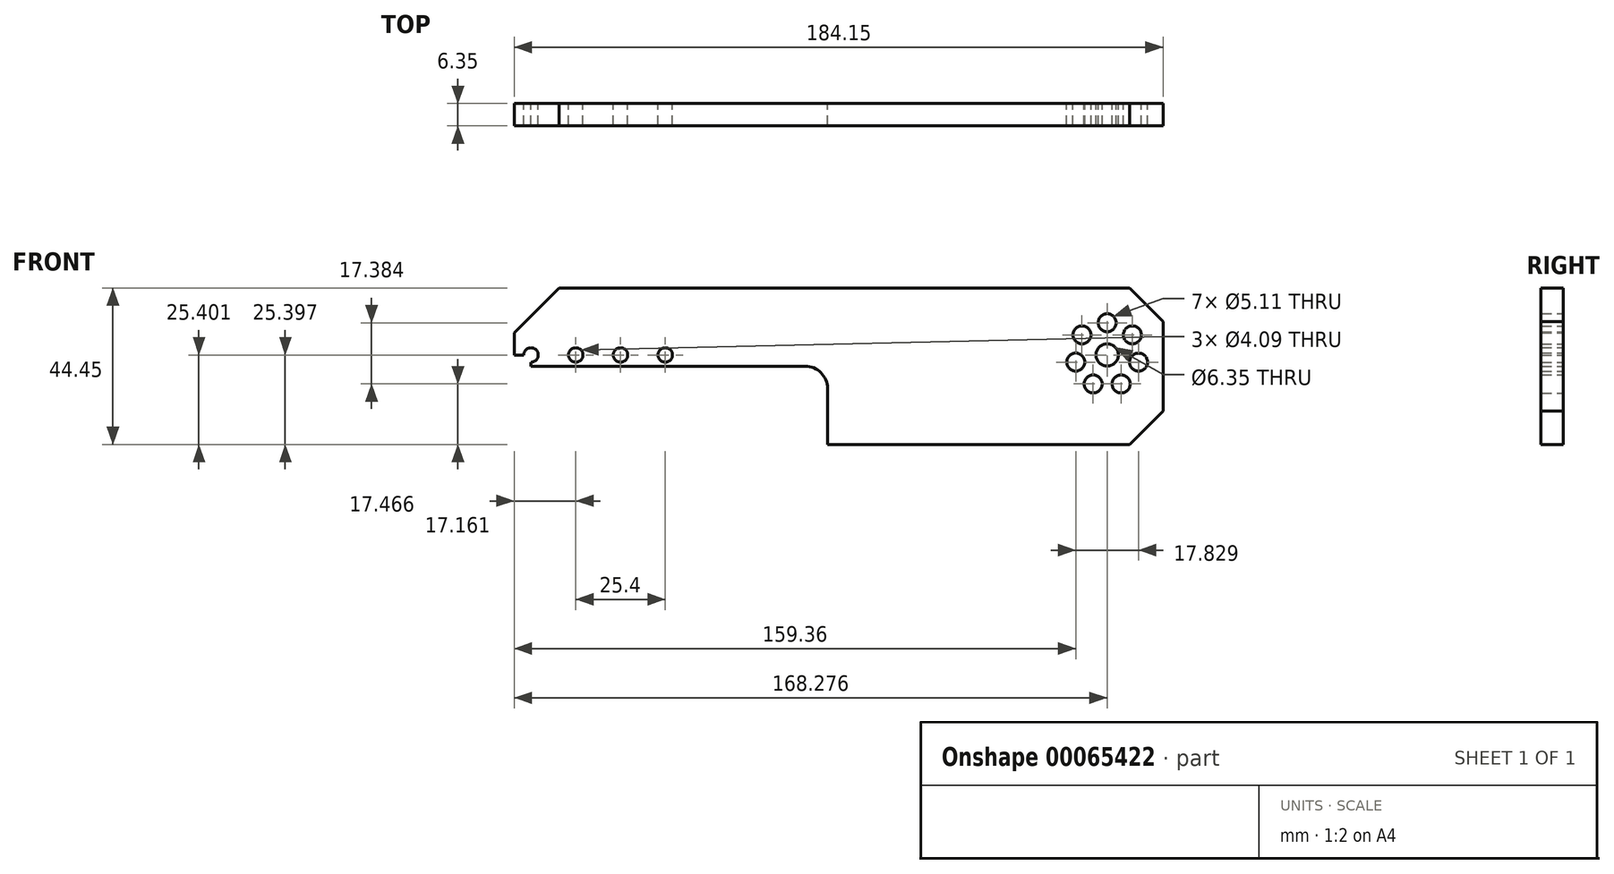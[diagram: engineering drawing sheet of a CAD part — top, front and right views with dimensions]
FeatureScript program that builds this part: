
annotation { "Feature Type Name" : "Feature", "Feature Type Description" : "" }
export const myFeature = defineFeature(function(context is Context, id is Id, definition is map)
    precondition{}
    {
        {
            var Q0;
            Q0=qCreatedBy(makeId("Front.planeOp"),FACE);
            var sketch = newSketch(context, id + "F0", { "sketchPlane" : qUnion([Q0])});
            skLineSegment(sketch, "E0", {"start": v(-93.68, 27.13) * mm, "end": v(68.25, 27.13) * mm});
            skLineSegment(sketch, "E1", {"start": v(-93.68, 27.13) * mm, "end": v(-106.38, 14.43) * mm});
            skLineSegment(sketch, "E2", {"start": v(68.25, 27.13) * mm, "end": v(77.77, 17.6) * mm});
            skLineSegment(sketch, "E3", {"start": v(-106.38, 14.43) * mm, "end": v(-106.38, 4.9) * mm});
            skLineSegment(sketch, "E4", {"start": v(-106.38, 4.9) * mm, "end": v(-23.83, 4.9) * mm});
            skLineSegment(sketch, "E5", {"start": v(-23.83, 4.9) * mm, "end": v(-23.83, -1.45) * mm});
            skArc(sketch, "E6", {"start": v(-23.83, 4.9) * mm, "mid": v(-19.34, 3.04) * mm, "end": v(-17.48, -1.45) * mm});
            skLineSegment(sketch, "E7", {"start": v(-17.48, -1.45) * mm, "end": v(-17.48, -17.32) * mm});
            skLineSegment(sketch, "E8", {"start": v(-17.48, -17.32) * mm, "end": v(68.25, -17.32) * mm});
            skLineSegment(sketch, "E9", {"start": v(68.25, -17.32) * mm, "end": v(77.77, -7.8) * mm});
            skLineSegment(sketch, "E10", {"start": v(77.77, 17.6) * mm, "end": v(77.77, -7.8) * mm});
            skLineSegment(sketch, "E11", {"start": v(77.77, 8.08) * mm, "end": v(61.9, 8.08) * mm});
            skCircle(sketch, "E12", {"center": v(61.9, 8.08) * mm, "radius": 3.18 * mm});
            skLineSegment(sketch, "E13", {"start": v(77.77, 27.13) * mm, "end": v(77.77, 17.22) * mm});
            skLineSegment(sketch, "E14", {"start": v(77.77, 17.22) * mm, "end": v(61.9, 17.23) * mm});
            skLineSegment(sketch, "E15.anchor1", {"start": v(61.9, 8.08) * mm, "end": v(61.9, 17.23) * mm, "construction": true});
            skLineSegment(sketch, "E15.anchor2", {"start": v(61.9, 8.08) * mm, "end": v(52.26, 15.77) * mm, "construction": true});
            skLineSegment(sketch, "E16.bottom", {"start": v(-106.38, 4.9) * mm, "end": v(-101.61, 4.9) * mm});
            skLineSegment(sketch, "E16.top", {"start": v(-106.38, 8.08) * mm, "end": v(-101.61, 8.08) * mm});
            skLineSegment(sketch, "E16.left", {"start": v(-106.38, 4.9) * mm, "end": v(-106.38, 8.08) * mm});
            skLineSegment(sketch, "E16.right", {"start": v(-101.61, 4.9) * mm, "end": v(-101.61, 8.08) * mm});
            skCircle(sketch, "E17", {"center": v(-101.61, 8.08) * mm, "radius": 2.04 * mm});
            skLineSegment(sketch, "E18.1.0.0", {"start": v(-93.68, 4.9) * mm, "end": v(-11.13, 4.9) * mm});
            skCircle(sketch, "E18.1.0.1", {"center": v(-88.91, 8.08) * mm, "radius": 2.04 * mm});
            skLineSegment(sketch, "E18.2.0.0", {"start": v(-80.98, 4.9) * mm, "end": v(1.57, 4.9) * mm});
            skCircle(sketch, "E18.2.0.1", {"center": v(-76.21, 8.08) * mm, "radius": 2.04 * mm});
            skLineSegment(sketch, "E18.3.0.0", {"start": v(-68.28, 4.9) * mm, "end": v(14.27, 4.9) * mm});
            skCircle(sketch, "E18.3.0.1", {"center": v(-63.51, 8.08) * mm, "radius": 2.04 * mm});
            skLineSegment(sketch, "E18.direction1", {"start": v(-106.38, 4.9) * mm, "end": v(-93.68, 4.9) * mm, "construction": true});
            skCircle(sketch, "E19", {"center": v(61.9, 17.23) * mm, "radius": 2.55 * mm});
            skCircle(sketch, "E20.1.0", {"center": v(54.75, 13.78) * mm, "radius": 2.55 * mm});
            skCircle(sketch, "E20.2.0", {"center": v(52.98, 6.05) * mm, "radius": 2.55 * mm});
            skCircle(sketch, "E20.3.0", {"center": v(57.93, -0.16) * mm, "radius": 2.55 * mm});
            skCircle(sketch, "E20.4.0", {"center": v(65.86, -0.16) * mm, "radius": 2.55 * mm});
            skCircle(sketch, "E20.5.0", {"center": v(70.8, 6.04) * mm, "radius": 2.55 * mm});
            skCircle(sketch, "E20.6.0", {"center": v(69.05, 13.78) * mm, "radius": 2.55 * mm});
            skSolve(sketch);
        }
        {
            var Q0;
            {var subQ14=sQuery(id+"F0.wireOp",EDGE,"E0");Q0=makeQuery(id+"F0.imprint","IMPRINT",FACE,{"disambiguationData":[TD([[makeQuery(id+"F0.imprint","IMPRINT",EDGE,{"derivedFrom":subQ14}),-1.0]])]});}
            var Q1;
            {var subQ1=sQuery(id+"F0.wireOp",EDGE,"E16.bottom");Q1=makeQuery(id+"F0.imprint","IMPRINT",FACE,{"disambiguationData":[TD([[makeQuery(id+"F0.imprint","IMPRINT",EDGE,{"derivedFrom":subQ1}),1.0]])]});}
            extrude(context, id + "F1", {"entities" : qUnion([Q0, Q1]), "depth" : 6.35 * mm});
        }
    });
